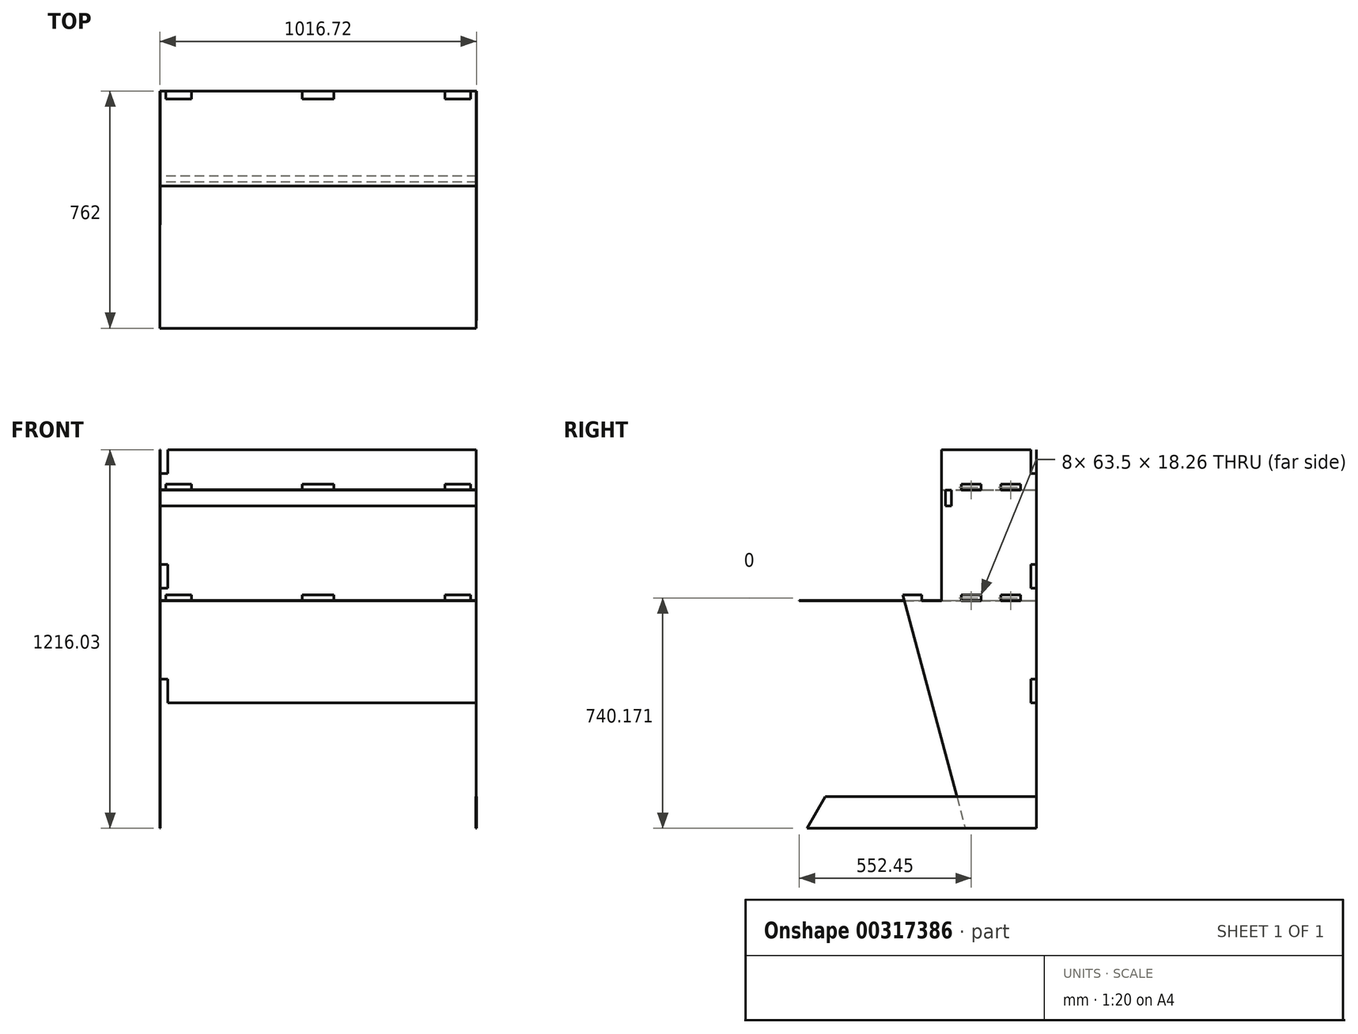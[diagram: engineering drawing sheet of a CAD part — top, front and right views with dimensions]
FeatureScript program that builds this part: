
annotation { "Feature Type Name" : "Feature", "Feature Type Description" : "" }
export const myFeature = defineFeature(function(context is Context, id is Id, definition is map)
    precondition{}
    {
        {
            assignVariable(context, id + "F0", {"name" : "T", "anyValue" : .719});
        }
        {
            var Q0;
            Q0=qCreatedBy(makeId("Top.planeOp"),FACE);
            var sketch = newSketch(context, id + "F1", { "sketchPlane" : qUnion([Q0])});
            skLineSegment(sketch, "E0.bottom", {"start": v(-508, 381) * mm, "end": v(508, 381) * mm});
            skLineSegment(sketch, "E0.top", {"start": v(-508, -381) * mm, "end": v(508, -381) * mm});
            skLineSegment(sketch, "E0.left", {"start": v(-508, 381) * mm, "end": v(-508, -381) * mm});
            skLineSegment(sketch, "E0.right", {"start": v(508, 381) * mm, "end": v(508, -381) * mm});
            skLineSegment(sketch, "E1", {"start": v(0, 0) * mm, "end": v(0, 287.9) * mm, "construction": true});
            skLineSegment(sketch, "E2", {"start": v(0, 0) * mm, "end": v(461.48, 0) * mm, "construction": true});
            skSolve(sketch);
        }
        {
            var Q0;
            Q0 = qSketchRegion(id + "F1", true);
            extrude(context, id + "F2", {"entities" : qUnion([Q0]), "depth" : (getVariable(context, 'T')) * mm});
        }
        {
            var Q0;
            Q0=makeQuery(id+"F2.opExtrude","SWEPT_FACE",FACE,{"disambiguationData":[OSD([sQuery(id+"F1.wireOp",EDGE,"E0.right")])]});
            var sketch = newSketch(context, id + "F3", { "sketchPlane" : qUnion([Q0])});
            skLineSegment(sketch, "E3.0", {"start": v(381, 18.26) * mm, "end": v(76.2, 18.26) * mm, "construction": true});
            skLineSegment(sketch, "E3.1", {"start": v(381, 18.26) * mm, "end": v(381, 0) * mm, "construction": true});
            skLineSegment(sketch, "E3.2", {"start": v(381, 0) * mm, "end": v(-381, 0) * mm, "construction": true});
            skLineSegment(sketch, "E4", {"start": v(381, 484.99) * mm, "end": v(381, -731.04) * mm});
            skLineSegment(sketch, "E5", {"start": v(381, 484.99) * mm, "end": v(76.2, 484.99) * mm});
            skLineSegment(sketch, "E6", {"start": v(76.2, 484.99) * mm, "end": v(76.2, 18.26) * mm});
            skLineSegment(sketch, "E7", {"start": v(12.7, 18.26) * mm, "end": v(-48.37, 18.26) * mm});
            skLineSegment(sketch, "E8", {"start": v(-48.37, 18.26) * mm, "end": v(152.4, -731.04) * mm});
            skLineSegment(sketch, "E9", {"start": v(152.4, -731.04) * mm, "end": v(381, -731.04) * mm});
            skLineSegment(sketch, "E10.bottom", {"start": v(12.7, 0) * mm, "end": v(76.2, 0) * mm});
            skLineSegment(sketch, "E10.left", {"start": v(12.7, 0) * mm, "end": v(12.7, 18.26) * mm});
            skLineSegment(sketch, "E10.right", {"start": v(76.2, 0) * mm, "end": v(76.2, 18.26) * mm});
            skLineSegment(sketch, "E11.bottom", {"start": v(139.7, 0) * mm, "end": v(203.2, 0) * mm});
            skLineSegment(sketch, "E11.top", {"start": v(139.7, 18.26) * mm, "end": v(203.2, 18.26) * mm});
            skLineSegment(sketch, "E11.left", {"start": v(139.7, 0) * mm, "end": v(139.7, 18.26) * mm});
            skLineSegment(sketch, "E11.right", {"start": v(203.2, 0) * mm, "end": v(203.2, 18.26) * mm});
            skLineSegment(sketch, "E12.bottom", {"start": v(266.7, 0) * mm, "end": v(330.2, 0) * mm});
            skLineSegment(sketch, "E12.top", {"start": v(266.7, 18.26) * mm, "end": v(330.2, 18.26) * mm});
            skLineSegment(sketch, "E12.left", {"start": v(266.7, 0) * mm, "end": v(266.7, 18.26) * mm});
            skLineSegment(sketch, "E12.right", {"start": v(330.2, 0) * mm, "end": v(330.2, 18.26) * mm});
            skLineSegment(sketch, "E13.trimOffspring", {"start": v(12.7, 18.26) * mm, "end": v(-381, 18.26) * mm, "construction": true});
            skLineSegment(sketch, "E14", {"start": v(381, 373.86) * mm, "end": v(76.2, 373.86) * mm, "construction": true});
            skLineSegment(sketch, "E15.bottom", {"start": v(330.2, 373.86) * mm, "end": v(266.7, 373.86) * mm});
            skLineSegment(sketch, "E16.bottom", {"start": v(203.2, 373.86) * mm, "end": v(139.7, 373.86) * mm});
            skLineSegment(sketch, "E17.top", {"start": v(88.9, 304.8) * mm, "end": v(107.16, 304.8) * mm});
            skLineSegment(sketch, "E17.left", {"start": v(88.9, 355.6) * mm, "end": v(88.9, 304.8) * mm});
            skLineSegment(sketch, "E17.right", {"start": v(107.16, 355.6) * mm, "end": v(107.16, 304.8) * mm});
            skLineSegment(sketch, "E18.bottom", {"start": v(139.7, 373.86) * mm, "end": v(203.2, 373.86) * mm});
            skLineSegment(sketch, "E18.top", {"start": v(139.7, 355.6) * mm, "end": v(203.2, 355.6) * mm});
            skLineSegment(sketch, "E18.left", {"start": v(139.7, 373.86) * mm, "end": v(139.7, 355.6) * mm});
            skLineSegment(sketch, "E18.right", {"start": v(203.2, 373.86) * mm, "end": v(203.2, 355.6) * mm});
            skLineSegment(sketch, "E19.bottom", {"start": v(266.7, 373.86) * mm, "end": v(330.2, 373.86) * mm});
            skLineSegment(sketch, "E19.top", {"start": v(266.7, 355.6) * mm, "end": v(330.2, 355.6) * mm});
            skLineSegment(sketch, "E19.left", {"start": v(266.7, 373.86) * mm, "end": v(266.7, 355.6) * mm});
            skLineSegment(sketch, "E19.right", {"start": v(330.2, 373.86) * mm, "end": v(330.2, 355.6) * mm});
            skLineSegment(sketch, "E20", {"start": v(107.16, 355.6) * mm, "end": v(88.9, 355.6) * mm});
            skSolve(sketch);
        }
        {
            var Q0;
            Q0 = qSketchRegion(id + "F3", true);
            extrude(context, id + "F4", {"entities" : qUnion([Q0]), "oppositeDirection" : true, "depth" : (getVariable(context, 'T')) * mm});
        }
        {
            var Q0;
            Q0=makeQuery(id+"F2.opExtrude","SWEPT_FACE",FACE,{"disambiguationData":[OSD([sQuery(id+"F1.wireOp",EDGE,"E0.left")])]});
            var sketch = newSketch(context, id + "F5", { "sketchPlane" : qUnion([Q0])});
            skLineSegment(sketch, "E21.0", {"start": v(-381, 484.99) * mm, "end": v(-76.2, 484.99) * mm});
            skLineSegment(sketch, "E21.1", {"start": v(-381, 484.99) * mm, "end": v(-381, -731.04) * mm});
            skLineSegment(sketch, "E21.2", {"start": v(-76.2, 484.99) * mm, "end": v(-76.2, 18.26) * mm});
            skLineSegment(sketch, "E21.3", {"start": v(-152.4, -731.04) * mm, "end": v(-381, -731.04) * mm});
            skLineSegment(sketch, "E21.4", {"start": v(48.37, 18.26) * mm, "end": v(-152.4, -731.04) * mm});
            skLineSegment(sketch, "E22", {"start": v(48.37, 18.26) * mm, "end": v(-76.2, 18.26) * mm});
            skSolve(sketch);
        }
        {
            var Q0;
            Q0 = qSketchRegion(id + "F5", true);
            extrude(context, id + "F6", {"entities" : qUnion([Q0]), "oppositeDirection" : true, "depth" : (getVariable(context, 'T')) * mm});
        }
        {
            var Q0;
            Q0=makeQuery(id+"F2.opExtrude","SWEPT_FACE",FACE,{"disambiguationData":[OSD([sQuery(id+"F1.wireOp",EDGE,"E0.bottom")])]});
            var sketch = newSketch(context, id + "F7", { "sketchPlane" : qUnion([Q0])});
            skLineSegment(sketch, "E23.0", {"start": v(-508, 484.99) * mm, "end": v(-508, -731.04) * mm, "construction": true});
            skLineSegment(sketch, "E23.2", {"start": v(508, 18.26) * mm, "end": v(-508, 18.26) * mm, "construction": true});
            skLineSegment(sketch, "E24.0", {"start": v(508, 484.99) * mm, "end": v(508, -731.04) * mm, "construction": true});
            skLineSegment(sketch, "E25.bottom", {"start": v(-508, 484.99) * mm, "end": v(508, 484.99) * mm});
            skLineSegment(sketch, "E25.top", {"start": v(-508, -327.81) * mm, "end": v(508, -327.81) * mm});
            skLineSegment(sketch, "E25.left", {"start": v(-508, 484.99) * mm, "end": v(-508, -327.81) * mm});
            skLineSegment(sketch, "E25.right", {"start": v(508, 484.99) * mm, "end": v(508, -327.81) * mm});
            skSolve(sketch);
        }
        {
            var Q0;
            Q0 = qSketchRegion(id + "F7", true);
            extrude(context, id + "F8", {"entities" : qUnion([Q0]), "oppositeDirection" : true, "depth" : (getVariable(context, 'T')) * mm});
        }
        {
            var Q0;
            Q0=qCreatedBy(makeId("Top.planeOp"),FACE);
            cPlane(context, id + "F9", {"entities" : qUnion([Q0]), "cplaneType" : CPlaneType.OFFSET, "offset" : 355.6 * mm, "width" : 152.4 * mm, "height" : 152.4 * mm});
        }
        {
            var Q0;
            Q0=qCreatedBy(id+"F9.planeOp",FACE);
            var sketch = newSketch(context, id + "F10", { "sketchPlane" : qUnion([Q0])});
            skLineSegment(sketch, "E26.0", {"start": v(508, 381) * mm, "end": v(508, 76.2) * mm});
            skLineSegment(sketch, "E26.1", {"start": v(-508, 381) * mm, "end": v(-508, 76.2) * mm});
            skLineSegment(sketch, "E27", {"start": v(508, 381) * mm, "end": v(-508, 381) * mm});
            skLineSegment(sketch, "E28", {"start": v(508, 76.2) * mm, "end": v(-508, 76.2) * mm});
            skSolve(sketch);
        }
        {
            var Q0;
            Q0 = qSketchRegion(id + "F10", true);
            extrude(context, id + "F11", {"entities" : qUnion([Q0]), "depth" : (getVariable(context, 'T')) * mm});
        }
        {
            var Q0;
            Q0=makeQuery(id+"F11.opExtrude","CAP_FACE",FACE,{"disambiguationData":[OSD([sQuery(id+"F10.wireOp",EDGE,"E26.0"),sQuery(id+"F10.wireOp",EDGE,"E26.1"),sQuery(id+"F10.wireOp",EDGE,"E27"),sQuery(id+"F10.wireOp",EDGE,"E28")])],"isStart":true});
            var sketch = newSketch(context, id + "F12", { "sketchPlane" : qUnion([Q0])});
            skLineSegment(sketch, "E29.0", {"start": v(508, -76.2) * mm, "end": v(-508, -76.2) * mm, "construction": true});
            skLineSegment(sketch, "E30.0", {"start": v(508, -381) * mm, "end": v(508, -76.2) * mm, "construction": true});
            skLineSegment(sketch, "E30.1", {"start": v(-508, -381) * mm, "end": v(-508, -76.2) * mm, "construction": true});
            skLineSegment(sketch, "E31.bottom", {"start": v(508, -88.9) * mm, "end": v(-508, -88.9) * mm});
            skLineSegment(sketch, "E31.top", {"start": v(508, -107.16) * mm, "end": v(-508, -107.16) * mm});
            skLineSegment(sketch, "E31.left", {"start": v(508, -88.9) * mm, "end": v(508, -107.16) * mm});
            skLineSegment(sketch, "E31.right", {"start": v(-508, -88.9) * mm, "end": v(-508, -107.16) * mm});
            skSolve(sketch);
        }
        {
            var Q0;
            Q0 = qSketchRegion(id + "F12", true);
            extrude(context, id + "F13", {"entities" : qUnion([Q0]), "depth" : 50.8 * mm});
        }
        {
            var Q0;
            Q0=makeQuery(id+"F4.opExtrude","CAP_FACE",FACE,{"disambiguationData":[OSD([sQuery(id+"F3.wireOp",EDGE,"E4"),sQuery(id+"F3.wireOp",EDGE,"E5"),sQuery(id+"F3.wireOp",EDGE,"E6"),sQuery(id+"F3.wireOp",EDGE,"E7"),sQuery(id+"F3.wireOp",EDGE,"E8"),sQuery(id+"F3.wireOp",EDGE,"E9")])],"isStart":true});
            var sketch = newSketch(context, id + "F14", { "sketchPlane" : qUnion([Q0])});
            skLineSegment(sketch, "E32.0", {"start": v(-48.37, 18.26) * mm, "end": v(152.4, -731.04) * mm, "construction": true});
            skLineSegment(sketch, "E32.1", {"start": v(152.4, -731.04) * mm, "end": v(381, -731.04) * mm, "construction": true});
            skLineSegment(sketch, "E33", {"start": v(152.4, -731.04) * mm, "end": v(-355.6, -731.04) * mm});
            skLineSegment(sketch, "E34", {"start": v(-355.6, -731.04) * mm, "end": v(-296.94, -629.44) * mm});
            skLineSegment(sketch, "E35", {"start": v(-296.94, -629.44) * mm, "end": v(125.18, -629.44) * mm});
            skLineSegment(sketch, "E36", {"start": v(125.18, -629.44) * mm, "end": v(152.4, -731.04) * mm});
            skSolve(sketch);
        }
        {
            var Q0;
            Q0 = qSketchRegion(id + "F14", true);
            extrude(context, id + "F15", {"entities" : qUnion([Q0]), "oppositeDirection" : true, "depth" : (getVariable(context, 'T')) * mm});
        }
        {
            var Q0;
            Q0=makeQuery(id+"F4.opExtrude","CAP_FACE",FACE,{"disambiguationData":[OSD([sQuery(id+"F3.wireOp",EDGE,"E4"),sQuery(id+"F3.wireOp",EDGE,"E5"),sQuery(id+"F3.wireOp",EDGE,"E6"),sQuery(id+"F3.wireOp",EDGE,"E7"),sQuery(id+"F3.wireOp",EDGE,"E8"),sQuery(id+"F3.wireOp",EDGE,"E9")])],"isStart":true});
            var sketch = newSketch(context, id + "F16", { "sketchPlane" : qUnion([Q0])});
            skLineSegment(sketch, "E37.0", {"start": v(381, 484.99) * mm, "end": v(381, -447.78) * mm, "construction": true});
            skLineSegment(sketch, "E37.1", {"start": v(152.4, -731.04) * mm, "end": v(381, -731.04) * mm, "construction": true});
            skLineSegment(sketch, "E37.2", {"start": v(152.4, -731.04) * mm, "end": v(-355.6, -731.04) * mm, "construction": true});
            skLineSegment(sketch, "E37.3", {"start": v(-355.6, -731.04) * mm, "end": v(-296.94, -629.44) * mm});
            skLineSegment(sketch, "E37.4", {"start": v(-296.94, -629.44) * mm, "end": v(125.18, -629.44) * mm, "construction": true});
            skLineSegment(sketch, "E38", {"start": v(381, -629.44) * mm, "end": v(381, -731.04) * mm});
            skLineSegment(sketch, "E39", {"start": v(-355.6, -731.04) * mm, "end": v(381, -731.04) * mm});
            skLineSegment(sketch, "E40", {"start": v(-296.94, -629.44) * mm, "end": v(381, -629.44) * mm});
            skLineSegment(sketch, "E41.trimOffspring", {"start": v(381, -629.44) * mm, "end": v(381, -731.04) * mm, "construction": true});
            skSolve(sketch);
        }
        {
            var Q0;
            Q0 = qSketchRegion(id + "F16", true);
            var Q1;
            Q1 = qConstructionFilter(qBodyType(qCreatedBy(id + "F16" ,EDGE), BodyType.WIRE), ConstructionObject.NO);
            extrude(context, id + "F17", {"entities" : qUnion([Q0]), "surfaceEntities" : qUnion([Q1]), "depth" : (getVariable(context, 'T')) * mm});
        }
        {
            var Q0;
            Q0=makeQuery(id+"F4.opExtrude","CAP_FACE",FACE,{"disambiguationData":[OSD([sQuery(id+"F3.wireOp",EDGE,"E4"),sQuery(id+"F3.wireOp",EDGE,"E5"),sQuery(id+"F3.wireOp",EDGE,"E6"),sQuery(id+"F3.wireOp",EDGE,"E7"),sQuery(id+"F3.wireOp",EDGE,"E8"),sQuery(id+"F3.wireOp",EDGE,"E9")])],"isStart":false});
            var sketch = newSketch(context, id + "F18", { "sketchPlane" : qUnion([Q0])});
            skLineSegment(sketch, "E42.0", {"start": v(355.6, -731.04) * mm, "end": v(-381, -731.04) * mm});
            skLineSegment(sketch, "E42.1", {"start": v(-381, -629.44) * mm, "end": v(-381, -731.04) * mm});
            skLineSegment(sketch, "E42.2", {"start": v(296.94, -629.44) * mm, "end": v(-381, -629.44) * mm});
            skLineSegment(sketch, "E42.3", {"start": v(355.6, -731.04) * mm, "end": v(296.94, -629.44) * mm});
            skSolve(sketch);
        }
        {
            var Q0;
            Q0 = qSketchRegion(id + "F18", true);
            extrude(context, id + "F19", {"entities" : qUnion([Q0]), "depth" : (getVariable(context, 'T')) * mm});
        }
        {
            var Q0;
            Q0=makeQuery(id+"F4.opExtrude","SWEPT_BODY",BODY,{"disambiguationData":[OSD([sQuery(id+"F3.wireOp",EDGE,"E4"),sQuery(id+"F3.wireOp",EDGE,"E5"),sQuery(id+"F3.wireOp",EDGE,"E6"),sQuery(id+"F3.wireOp",EDGE,"E7"),sQuery(id+"F3.wireOp",EDGE,"E8"),sQuery(id+"F3.wireOp",EDGE,"E9"),sQuery(id+"F3.wireOp",EDGE,"E10.bottom"),sQuery(id+"F3.wireOp",EDGE,"E10.left"),sQuery(id+"F3.wireOp",EDGE,"E10.right"),sQuery(id+"F3.wireOp",EDGE,"E11.bottom"),sQuery(id+"F3.wireOp",EDGE,"E11.top"),sQuery(id+"F3.wireOp",EDGE,"E11.left"),sQuery(id+"F3.wireOp",EDGE,"E11.right"),sQuery(id+"F3.wireOp",EDGE,"E12.bottom"),sQuery(id+"F3.wireOp",EDGE,"E12.top"),sQuery(id+"F3.wireOp",EDGE,"E12.left"),sQuery(id+"F3.wireOp",EDGE,"E12.right"),sQuery(id+"F3.wireOp",EDGE,"E17.top"),sQuery(id+"F3.wireOp",EDGE,"E17.left"),sQuery(id+"F3.wireOp",EDGE,"E17.right"),sQuery(id+"F3.wireOp",EDGE,"E18.bottom"),sQuery(id+"F3.wireOp",EDGE,"E18.top"),sQuery(id+"F3.wireOp",EDGE,"E18.left"),sQuery(id+"F3.wireOp",EDGE,"E18.right"),sQuery(id+"F3.wireOp",EDGE,"E19.bottom"),sQuery(id+"F3.wireOp",EDGE,"E19.top"),sQuery(id+"F3.wireOp",EDGE,"E19.left"),sQuery(id+"F3.wireOp",EDGE,"E19.right"),sQuery(id+"F3.wireOp",EDGE,"E20")])]});
            var Q1;
            Q1=makeQuery(id+"F11.opExtrude","SWEPT_BODY",BODY,{"disambiguationData":[OSD([sQuery(id+"F10.wireOp",EDGE,"E26.0"),sQuery(id+"F10.wireOp",EDGE,"E26.1"),sQuery(id+"F10.wireOp",EDGE,"E27"),sQuery(id+"F10.wireOp",EDGE,"E28")])]});
            booleanBodies(context, id + "F20", {"operationType" : BooleanOperationType.SUBTRACTION, "tools" : qUnion([Q0]), "targets" : qUnion([Q1]), "keepTools" : true});
        }
        {
            var Q0;
            Q0=makeQuery(id+"F4.opExtrude","SWEPT_BODY",BODY,{"disambiguationData":[OSD([sQuery(id+"F3.wireOp",EDGE,"E4"),sQuery(id+"F3.wireOp",EDGE,"E5"),sQuery(id+"F3.wireOp",EDGE,"E6"),sQuery(id+"F3.wireOp",EDGE,"E7"),sQuery(id+"F3.wireOp",EDGE,"E8"),sQuery(id+"F3.wireOp",EDGE,"E9"),sQuery(id+"F3.wireOp",EDGE,"E10.bottom"),sQuery(id+"F3.wireOp",EDGE,"E10.left"),sQuery(id+"F3.wireOp",EDGE,"E10.right"),sQuery(id+"F3.wireOp",EDGE,"E11.bottom"),sQuery(id+"F3.wireOp",EDGE,"E11.top"),sQuery(id+"F3.wireOp",EDGE,"E11.left"),sQuery(id+"F3.wireOp",EDGE,"E11.right"),sQuery(id+"F3.wireOp",EDGE,"E12.bottom"),sQuery(id+"F3.wireOp",EDGE,"E12.top"),sQuery(id+"F3.wireOp",EDGE,"E12.left"),sQuery(id+"F3.wireOp",EDGE,"E12.right"),sQuery(id+"F3.wireOp",EDGE,"E17.top"),sQuery(id+"F3.wireOp",EDGE,"E17.left"),sQuery(id+"F3.wireOp",EDGE,"E17.right"),sQuery(id+"F3.wireOp",EDGE,"E18.bottom"),sQuery(id+"F3.wireOp",EDGE,"E18.top"),sQuery(id+"F3.wireOp",EDGE,"E18.left"),sQuery(id+"F3.wireOp",EDGE,"E18.right"),sQuery(id+"F3.wireOp",EDGE,"E19.bottom"),sQuery(id+"F3.wireOp",EDGE,"E19.top"),sQuery(id+"F3.wireOp",EDGE,"E19.left"),sQuery(id+"F3.wireOp",EDGE,"E19.right"),sQuery(id+"F3.wireOp",EDGE,"E20")])]});
            var Q1;
            Q1=makeQuery(id+"F2.opExtrude","SWEPT_BODY",BODY,{"disambiguationData":[OSD([sQuery(id+"F1.wireOp",EDGE,"E0.bottom"),sQuery(id+"F1.wireOp",EDGE,"E0.top"),sQuery(id+"F1.wireOp",EDGE,"E0.left"),sQuery(id+"F1.wireOp",EDGE,"E0.right")])]});
            booleanBodies(context, id + "F21", {"operationType" : BooleanOperationType.SUBTRACTION, "tools" : qUnion([Q0]), "targets" : qUnion([Q1]), "keepTools" : true});
        }
        {
            var Q0;
            Q0=makeQuery(id+"F6.opExtrude","CAP_FACE",FACE,{"disambiguationData":[OSD([sQuery(id+"F5.wireOp",EDGE,"E21.0"),sQuery(id+"F5.wireOp",EDGE,"E21.1"),sQuery(id+"F5.wireOp",EDGE,"E21.2"),sQuery(id+"F5.wireOp",EDGE,"E21.3"),sQuery(id+"F5.wireOp",EDGE,"E21.4"),sQuery(id+"F5.wireOp",EDGE,"RNXhw258-0f9s-xMxb-Sfib-8PFL4Zg6WHv6")])],"isStart":false});
            var sketch = newSketch(context, id + "F22", { "sketchPlane" : qUnion([Q0])});
            skLineSegment(sketch, "E43.0", {"start": v(266.7, 355.6) * mm, "end": v(330.2, 355.6) * mm});
            skLineSegment(sketch, "E43.1", {"start": v(266.7, 373.86) * mm, "end": v(266.7, 355.6) * mm});
            skLineSegment(sketch, "E43.2", {"start": v(266.7, 373.86) * mm, "end": v(330.2, 373.86) * mm});
            skLineSegment(sketch, "E43.3", {"start": v(330.2, 373.86) * mm, "end": v(330.2, 355.6) * mm});
            skLineSegment(sketch, "E43.4", {"start": v(203.2, 373.86) * mm, "end": v(203.2, 355.6) * mm});
            skLineSegment(sketch, "E43.5", {"start": v(139.7, 373.86) * mm, "end": v(203.2, 373.86) * mm});
            skLineSegment(sketch, "E43.6", {"start": v(139.7, 355.6) * mm, "end": v(203.2, 355.6) * mm});
            skLineSegment(sketch, "E43.7", {"start": v(139.7, 373.86) * mm, "end": v(139.7, 355.6) * mm});
            skLineSegment(sketch, "E43.8", {"start": v(107.16, 355.6) * mm, "end": v(107.16, 304.8) * mm});
            skLineSegment(sketch, "E43.9", {"start": v(107.16, 355.6) * mm, "end": v(88.9, 355.6) * mm});
            skLineSegment(sketch, "E43.10", {"start": v(88.9, 355.6) * mm, "end": v(88.9, 304.8) * mm});
            skLineSegment(sketch, "E43.11", {"start": v(88.9, 304.8) * mm, "end": v(107.16, 304.8) * mm});
            skLineSegment(sketch, "E43.12", {"start": v(76.2, 0) * mm, "end": v(12.7, 0) * mm});
            skLineSegment(sketch, "E43.13", {"start": v(12.7, 0) * mm, "end": v(12.7, 18.26) * mm});
            skLineSegment(sketch, "E43.14", {"start": v(139.7, 0) * mm, "end": v(139.7, 18.26) * mm});
            skLineSegment(sketch, "E43.15", {"start": v(203.2, 0) * mm, "end": v(139.7, 0) * mm});
            skLineSegment(sketch, "E43.16", {"start": v(203.2, 18.26) * mm, "end": v(139.7, 18.26) * mm});
            skLineSegment(sketch, "E43.17", {"start": v(203.2, 0) * mm, "end": v(203.2, 18.26) * mm});
            skLineSegment(sketch, "E43.18", {"start": v(266.7, 0) * mm, "end": v(266.7, 18.26) * mm});
            skLineSegment(sketch, "E43.19", {"start": v(330.2, 0) * mm, "end": v(266.7, 0) * mm});
            skLineSegment(sketch, "E43.20", {"start": v(330.2, 18.26) * mm, "end": v(266.7, 18.26) * mm});
            skLineSegment(sketch, "E43.21", {"start": v(330.2, 0) * mm, "end": v(330.2, 18.26) * mm});
            skLineSegment(sketch, "E44", {"start": v(12.7, 18.26) * mm, "end": v(76.2, 18.26) * mm});
            skLineSegment(sketch, "E45", {"start": v(76.2, 18.26) * mm, "end": v(76.2, 0) * mm});
            skSolve(sketch);
        }
        {
            var Q0;
            Q0 = qSketchRegion(id + "F22", true);
            extrude(context, id + "F23", {"entities" : qUnion([Q0]), "operationType" : NewBodyOperationType.REMOVE, "oppositeDirection" : true, "depth" : 25.4 * mm});
        }
        {
            var Q0;
            Q0=makeQuery(id+"F6.opExtrude","SWEPT_BODY",BODY,{"disambiguationData":[OSD([sQuery(id+"F5.wireOp",EDGE,"E21.0"),sQuery(id+"F5.wireOp",EDGE,"E21.1"),sQuery(id+"F5.wireOp",EDGE,"E21.2"),sQuery(id+"F5.wireOp",EDGE,"E21.3"),sQuery(id+"F5.wireOp",EDGE,"E21.4"),sQuery(id+"F5.wireOp",EDGE,"E22")])]});
            var Q1;
            Q1=makeQuery(id+"F11.opExtrude","SWEPT_BODY",BODY,{"disambiguationData":[OSD([sQuery(id+"F10.wireOp",EDGE,"E26.0"),sQuery(id+"F10.wireOp",EDGE,"E26.1"),sQuery(id+"F10.wireOp",EDGE,"E27"),sQuery(id+"F10.wireOp",EDGE,"E28")])]});
            booleanBodies(context, id + "F24", {"operationType" : BooleanOperationType.SUBTRACTION, "tools" : qUnion([Q0]), "targets" : qUnion([Q1]), "keepTools" : true});
        }
        {
            var Q0;
            Q0=makeQuery(id+"F6.opExtrude","SWEPT_BODY",BODY,{"disambiguationData":[OSD([sQuery(id+"F5.wireOp",EDGE,"E21.0"),sQuery(id+"F5.wireOp",EDGE,"E21.1"),sQuery(id+"F5.wireOp",EDGE,"E21.2"),sQuery(id+"F5.wireOp",EDGE,"E21.3"),sQuery(id+"F5.wireOp",EDGE,"E21.4"),sQuery(id+"F5.wireOp",EDGE,"E22")])]});
            var Q1;
            Q1=makeQuery(id+"F2.opExtrude","SWEPT_BODY",BODY,{"disambiguationData":[OSD([sQuery(id+"F1.wireOp",EDGE,"E0.bottom"),sQuery(id+"F1.wireOp",EDGE,"E0.top"),sQuery(id+"F1.wireOp",EDGE,"E0.left"),sQuery(id+"F1.wireOp",EDGE,"E0.right")])]});
            booleanBodies(context, id + "F25", {"operationType" : BooleanOperationType.SUBTRACTION, "tools" : qUnion([Q0]), "targets" : qUnion([Q1]), "keepTools" : true});
        }
        {
            var Q0;
            Q0=makeQuery(id+"F4.opExtrude","CAP_FACE",FACE,{"disambiguationData":[OSD([sQuery(id+"F3.wireOp",EDGE,"E4"),sQuery(id+"F3.wireOp",EDGE,"E5"),sQuery(id+"F3.wireOp",EDGE,"E6"),sQuery(id+"F3.wireOp",EDGE,"E7"),sQuery(id+"F3.wireOp",EDGE,"E8"),sQuery(id+"F3.wireOp",EDGE,"E9"),sQuery(id+"F3.wireOp",EDGE,"E10.bottom"),sQuery(id+"F3.wireOp",EDGE,"E10.left"),sQuery(id+"F3.wireOp",EDGE,"E10.right"),sQuery(id+"F3.wireOp",EDGE,"E11.bottom"),sQuery(id+"F3.wireOp",EDGE,"E11.top"),sQuery(id+"F3.wireOp",EDGE,"E11.left"),sQuery(id+"F3.wireOp",EDGE,"E11.right"),sQuery(id+"F3.wireOp",EDGE,"E12.bottom"),sQuery(id+"F3.wireOp",EDGE,"E12.top"),sQuery(id+"F3.wireOp",EDGE,"E12.left"),sQuery(id+"F3.wireOp",EDGE,"E12.right"),sQuery(id+"F3.wireOp",EDGE,"E17.top"),sQuery(id+"F3.wireOp",EDGE,"E17.left"),sQuery(id+"F3.wireOp",EDGE,"E17.right"),sQuery(id+"F3.wireOp",EDGE,"E18.bottom"),sQuery(id+"F3.wireOp",EDGE,"E18.top"),sQuery(id+"F3.wireOp",EDGE,"E18.left"),sQuery(id+"F3.wireOp",EDGE,"E18.right"),sQuery(id+"F3.wireOp",EDGE,"E19.bottom"),sQuery(id+"F3.wireOp",EDGE,"E19.top"),sQuery(id+"F3.wireOp",EDGE,"E19.left"),sQuery(id+"F3.wireOp",EDGE,"E19.right"),sQuery(id+"F3.wireOp",EDGE,"E20")])],"isStart":true});
            var sketch = newSketch(context, id + "F26", { "sketchPlane" : qUnion([Q0])});
            skLineSegment(sketch, "E46.0", {"start": v(381, 484.99) * mm, "end": v(381, -731.04) * mm, "construction": true});
            skLineSegment(sketch, "E46.1", {"start": v(381, 484.99) * mm, "end": v(76.2, 484.99) * mm, "construction": true});
            skLineSegment(sketch, "E47.0", {"start": v(362.74, 484.99) * mm, "end": v(362.74, -327.81) * mm, "construction": true});
            skLineSegment(sketch, "E48.bottom", {"start": v(381, 484.99) * mm, "end": v(362.74, 484.99) * mm});
            skLineSegment(sketch, "E48.top", {"start": v(381, 408.79) * mm, "end": v(362.74, 408.79) * mm});
            skLineSegment(sketch, "E48.left", {"start": v(381, 484.99) * mm, "end": v(381, 408.79) * mm});
            skLineSegment(sketch, "E48.right", {"start": v(362.74, 484.99) * mm, "end": v(362.74, 408.79) * mm});
            skLineSegment(sketch, "E49.bottom", {"start": v(362.74, -327.81) * mm, "end": v(381, -327.81) * mm});
            skLineSegment(sketch, "E49.top", {"start": v(362.74, -251.61) * mm, "end": v(381, -251.61) * mm});
            skLineSegment(sketch, "E49.left", {"start": v(362.74, -327.81) * mm, "end": v(362.74, -251.61) * mm});
            skLineSegment(sketch, "E49.right", {"start": v(381, -327.81) * mm, "end": v(381, -251.61) * mm});
            skLineSegment(sketch, "E50.bottom", {"start": v(362.74, 116.69) * mm, "end": v(381, 116.69) * mm});
            skLineSegment(sketch, "E50.top", {"start": v(362.74, 40.49) * mm, "end": v(381, 40.49) * mm});
            skLineSegment(sketch, "E50.left", {"start": v(362.74, 116.69) * mm, "end": v(362.74, 40.49) * mm});
            skLineSegment(sketch, "E50.right", {"start": v(381, 116.69) * mm, "end": v(381, 40.49) * mm});
            skSolve(sketch);
        }
        {
            var Q0;
            Q0 = qSketchRegion(id + "F26", true);
            extrude(context, id + "F27", {"entities" : qUnion([Q0]), "operationType" : NewBodyOperationType.REMOVE, "oppositeDirection" : true, "depth" : (getVariable(context, 'T')) * mm});
        }
        {
            var Q0;
            Q0=makeQuery(id+"F4.opExtrude","SWEPT_BODY",BODY,{"disambiguationData":[OSD([sQuery(id+"F3.wireOp",EDGE,"E4"),sQuery(id+"F3.wireOp",EDGE,"E5"),sQuery(id+"F3.wireOp",EDGE,"E6"),sQuery(id+"F3.wireOp",EDGE,"E7"),sQuery(id+"F3.wireOp",EDGE,"E8"),sQuery(id+"F3.wireOp",EDGE,"E9"),sQuery(id+"F3.wireOp",EDGE,"E10.bottom"),sQuery(id+"F3.wireOp",EDGE,"E10.left"),sQuery(id+"F3.wireOp",EDGE,"E10.right"),sQuery(id+"F3.wireOp",EDGE,"E11.bottom"),sQuery(id+"F3.wireOp",EDGE,"E11.top"),sQuery(id+"F3.wireOp",EDGE,"E11.left"),sQuery(id+"F3.wireOp",EDGE,"E11.right"),sQuery(id+"F3.wireOp",EDGE,"E12.bottom"),sQuery(id+"F3.wireOp",EDGE,"E12.top"),sQuery(id+"F3.wireOp",EDGE,"E12.left"),sQuery(id+"F3.wireOp",EDGE,"E12.right"),sQuery(id+"F3.wireOp",EDGE,"E17.top"),sQuery(id+"F3.wireOp",EDGE,"E17.left"),sQuery(id+"F3.wireOp",EDGE,"E17.right"),sQuery(id+"F3.wireOp",EDGE,"E18.bottom"),sQuery(id+"F3.wireOp",EDGE,"E18.top"),sQuery(id+"F3.wireOp",EDGE,"E18.left"),sQuery(id+"F3.wireOp",EDGE,"E18.right"),sQuery(id+"F3.wireOp",EDGE,"E19.bottom"),sQuery(id+"F3.wireOp",EDGE,"E19.top"),sQuery(id+"F3.wireOp",EDGE,"E19.left"),sQuery(id+"F3.wireOp",EDGE,"E19.right"),sQuery(id+"F3.wireOp",EDGE,"E20")])]});
            var Q1;
            Q1=makeQuery(id+"F8.opExtrude","SWEPT_BODY",BODY,{"disambiguationData":[OSD([sQuery(id+"F7.wireOp",EDGE,"E25.bottom"),sQuery(id+"F7.wireOp",EDGE,"E25.top"),sQuery(id+"F7.wireOp",EDGE,"E25.left"),sQuery(id+"F7.wireOp",EDGE,"E25.right")])]});
            booleanBodies(context, id + "F28", {"operationType" : BooleanOperationType.SUBTRACTION, "tools" : qUnion([Q0]), "targets" : qUnion([Q1]), "keepTools" : true});
        }
        {
            var Q0;
            Q0=makeQuery(id+"F8.opExtrude","CAP_FACE",FACE,{"disambiguationData":[OSD([sQuery(id+"F7.wireOp",EDGE,"E25.bottom"),sQuery(id+"F7.wireOp",EDGE,"E25.top"),sQuery(id+"F7.wireOp",EDGE,"E25.left"),sQuery(id+"F7.wireOp",EDGE,"E25.right")])],"isStart":true});
            var sketch = newSketch(context, id + "F29", { "sketchPlane" : qUnion([Q0])});
            skLineSegment(sketch, "E51.0", {"start": v(-489.74, 373.86) * mm, "end": v(489.74, 373.86) * mm, "construction": true});
            skLineSegment(sketch, "E51.1", {"start": v(-489.74, 355.6) * mm, "end": v(489.74, 355.6) * mm, "construction": true});
            skLineSegment(sketch, "E51.2", {"start": v(489.74, 18.26) * mm, "end": v(-489.74, 18.26) * mm, "construction": true});
            skLineSegment(sketch, "E51.3", {"start": v(489.74, 0) * mm, "end": v(-489.74, 0) * mm, "construction": true});
            skLineSegment(sketch, "E52.bottom", {"start": v(-489.74, 373.86) * mm, "end": v(-407.19, 373.86) * mm});
            skLineSegment(sketch, "E52.top", {"start": v(-489.74, 355.6) * mm, "end": v(-407.19, 355.6) * mm});
            skLineSegment(sketch, "E52.left", {"start": v(-489.74, 373.86) * mm, "end": v(-489.74, 355.6) * mm});
            skLineSegment(sketch, "E52.right", {"start": v(-407.19, 373.86) * mm, "end": v(-407.19, 355.6) * mm});
            skLineSegment(sketch, "E53.bottom", {"start": v(489.74, 373.86) * mm, "end": v(407.19, 373.86) * mm});
            skLineSegment(sketch, "E53.top", {"start": v(489.74, 355.6) * mm, "end": v(407.19, 355.6) * mm});
            skLineSegment(sketch, "E53.left", {"start": v(489.74, 373.86) * mm, "end": v(489.74, 355.6) * mm});
            skLineSegment(sketch, "E53.right", {"start": v(407.19, 373.86) * mm, "end": v(407.19, 355.6) * mm});
            skLineSegment(sketch, "E54.bottom", {"start": v(-489.74, 18.26) * mm, "end": v(-407.19, 18.26) * mm});
            skLineSegment(sketch, "E54.top", {"start": v(-489.74, 0) * mm, "end": v(-407.19, 0) * mm});
            skLineSegment(sketch, "E54.left", {"start": v(-489.74, 18.26) * mm, "end": v(-489.74, 0) * mm});
            skLineSegment(sketch, "E54.right", {"start": v(-407.19, 18.26) * mm, "end": v(-407.19, 0) * mm});
            skLineSegment(sketch, "E55.bottom", {"start": v(-50.8, 373.86) * mm, "end": v(50.8, 373.86) * mm});
            skLineSegment(sketch, "E55.top", {"start": v(-50.8, 355.6) * mm, "end": v(50.8, 355.6) * mm});
            skLineSegment(sketch, "E55.left", {"start": v(-50.8, 373.86) * mm, "end": v(-50.8, 355.6) * mm});
            skLineSegment(sketch, "E55.right", {"start": v(50.8, 373.86) * mm, "end": v(50.8, 355.6) * mm});
            skLineSegment(sketch, "E56.bottom", {"start": v(-50.8, 18.26) * mm, "end": v(50.8, 18.26) * mm});
            skLineSegment(sketch, "E56.top", {"start": v(-50.8, 0) * mm, "end": v(50.8, 0) * mm});
            skLineSegment(sketch, "E56.left", {"start": v(-50.8, 18.26) * mm, "end": v(-50.8, 0) * mm});
            skLineSegment(sketch, "E56.right", {"start": v(50.8, 18.26) * mm, "end": v(50.8, 0) * mm});
            skLineSegment(sketch, "E57", {"start": v(489.74, 18.26) * mm, "end": v(407.19, 18.26) * mm});
            skLineSegment(sketch, "E58", {"start": v(407.19, 18.26) * mm, "end": v(407.19, 0) * mm});
            skLineSegment(sketch, "E59", {"start": v(407.19, 0) * mm, "end": v(489.74, 0) * mm});
            skLineSegment(sketch, "E60", {"start": v(489.74, 18.26) * mm, "end": v(489.74, 0) * mm});
            skSolve(sketch);
        }
        {
            var Q0;
            Q0 = qSketchRegion(id + "F29", true);
            extrude(context, id + "F30", {"entities" : qUnion([Q0]), "operationType" : NewBodyOperationType.REMOVE, "oppositeDirection" : true, "depth" : 25.4 * mm});
        }
        {
            var Q0;
            Q0=makeQuery(id+"F8.opExtrude","SWEPT_BODY",BODY,{"disambiguationData":[OSD([sQuery(id+"F7.wireOp",EDGE,"E25.bottom"),sQuery(id+"F7.wireOp",EDGE,"E25.top"),sQuery(id+"F7.wireOp",EDGE,"E25.left"),sQuery(id+"F7.wireOp",EDGE,"E25.right")])]});
            var Q1;
            Q1=makeQuery(id+"F11.opExtrude","SWEPT_BODY",BODY,{"disambiguationData":[OSD([sQuery(id+"F10.wireOp",EDGE,"E26.0"),sQuery(id+"F10.wireOp",EDGE,"E26.1"),sQuery(id+"F10.wireOp",EDGE,"E27"),sQuery(id+"F10.wireOp",EDGE,"E28")])]});
            booleanBodies(context, id + "F31", {"operationType" : BooleanOperationType.SUBTRACTION, "tools" : qUnion([Q0]), "targets" : qUnion([Q1]), "keepTools" : true});
        }
        {
            var Q0;
            Q0=makeQuery(id+"F8.opExtrude","SWEPT_BODY",BODY,{"disambiguationData":[OSD([sQuery(id+"F7.wireOp",EDGE,"E25.bottom"),sQuery(id+"F7.wireOp",EDGE,"E25.top"),sQuery(id+"F7.wireOp",EDGE,"E25.left"),sQuery(id+"F7.wireOp",EDGE,"E25.right")])]});
            var Q1;
            Q1=makeQuery(id+"F2.opExtrude","SWEPT_BODY",BODY,{"disambiguationData":[OSD([sQuery(id+"F1.wireOp",EDGE,"E0.bottom"),sQuery(id+"F1.wireOp",EDGE,"E0.top"),sQuery(id+"F1.wireOp",EDGE,"E0.left"),sQuery(id+"F1.wireOp",EDGE,"E0.right")])]});
            booleanBodies(context, id + "F32", {"operationType" : BooleanOperationType.SUBTRACTION, "tools" : qUnion([Q0]), "targets" : qUnion([Q1]), "keepTools" : true});
        }
        {
            var Q0;
            Q0=makeQuery(id+"F6.opExtrude","CAP_FACE",FACE,{"disambiguationData":[OSD([sQuery(id+"F5.wireOp",EDGE,"E21.0"),sQuery(id+"F5.wireOp",EDGE,"E21.1"),sQuery(id+"F5.wireOp",EDGE,"E21.2"),sQuery(id+"F5.wireOp",EDGE,"E21.3"),sQuery(id+"F5.wireOp",EDGE,"E21.4"),sQuery(id+"F5.wireOp",EDGE,"E22")])],"isStart":true});
            var sketch = newSketch(context, id + "F33", { "sketchPlane" : qUnion([Q0])});
            skLineSegment(sketch, "E61.0", {"start": v(-362.74, 484.99) * mm, "end": v(-362.74, 408.79) * mm});
            skLineSegment(sketch, "E61.1", {"start": v(-381, 484.99) * mm, "end": v(-381, 408.79) * mm});
            skLineSegment(sketch, "E61.2", {"start": v(-362.74, 484.99) * mm, "end": v(-381, 484.99) * mm});
            skLineSegment(sketch, "E61.3", {"start": v(-381, 408.79) * mm, "end": v(-362.74, 408.79) * mm});
            skLineSegment(sketch, "E61.4", {"start": v(-362.74, 116.69) * mm, "end": v(-381, 116.69) * mm});
            skLineSegment(sketch, "E61.5", {"start": v(-362.74, 116.69) * mm, "end": v(-362.74, 40.49) * mm});
            skLineSegment(sketch, "E61.6", {"start": v(-362.74, 40.49) * mm, "end": v(-381, 40.49) * mm});
            skLineSegment(sketch, "E61.7", {"start": v(-362.74, -251.61) * mm, "end": v(-381, -251.61) * mm});
            skLineSegment(sketch, "E61.8", {"start": v(-362.74, -327.81) * mm, "end": v(-362.74, -251.61) * mm});
            skLineSegment(sketch, "E61.9", {"start": v(-362.74, -327.81) * mm, "end": v(-381, -327.81) * mm});
            skLineSegment(sketch, "E62", {"start": v(-381, 116.69) * mm, "end": v(-381, 40.49) * mm});
            skLineSegment(sketch, "E63", {"start": v(-381, -251.61) * mm, "end": v(-381, -327.81) * mm});
            skSolve(sketch);
        }
        {
            var Q0;
            Q0 = qSketchRegion(id + "F33", true);
            extrude(context, id + "F34", {"entities" : qUnion([Q0]), "operationType" : NewBodyOperationType.REMOVE, "oppositeDirection" : true, "depth" : 25.4 * mm});
        }
        {
            var Q0;
            Q0=makeQuery(id+"F6.opExtrude","SWEPT_BODY",BODY,{"disambiguationData":[OSD([sQuery(id+"F5.wireOp",EDGE,"E21.0"),sQuery(id+"F5.wireOp",EDGE,"E21.1"),sQuery(id+"F5.wireOp",EDGE,"E21.2"),sQuery(id+"F5.wireOp",EDGE,"E21.3"),sQuery(id+"F5.wireOp",EDGE,"E21.4"),sQuery(id+"F5.wireOp",EDGE,"E22")])]});
            var Q1;
            Q1=makeQuery(id+"F8.opExtrude","SWEPT_BODY",BODY,{"disambiguationData":[OSD([sQuery(id+"F7.wireOp",EDGE,"E25.bottom"),sQuery(id+"F7.wireOp",EDGE,"E25.top"),sQuery(id+"F7.wireOp",EDGE,"E25.left"),sQuery(id+"F7.wireOp",EDGE,"E25.right")])]});
            booleanBodies(context, id + "F35", {"operationType" : BooleanOperationType.SUBTRACTION, "tools" : qUnion([Q0]), "targets" : qUnion([Q1]), "keepTools" : true});
        }
    });
